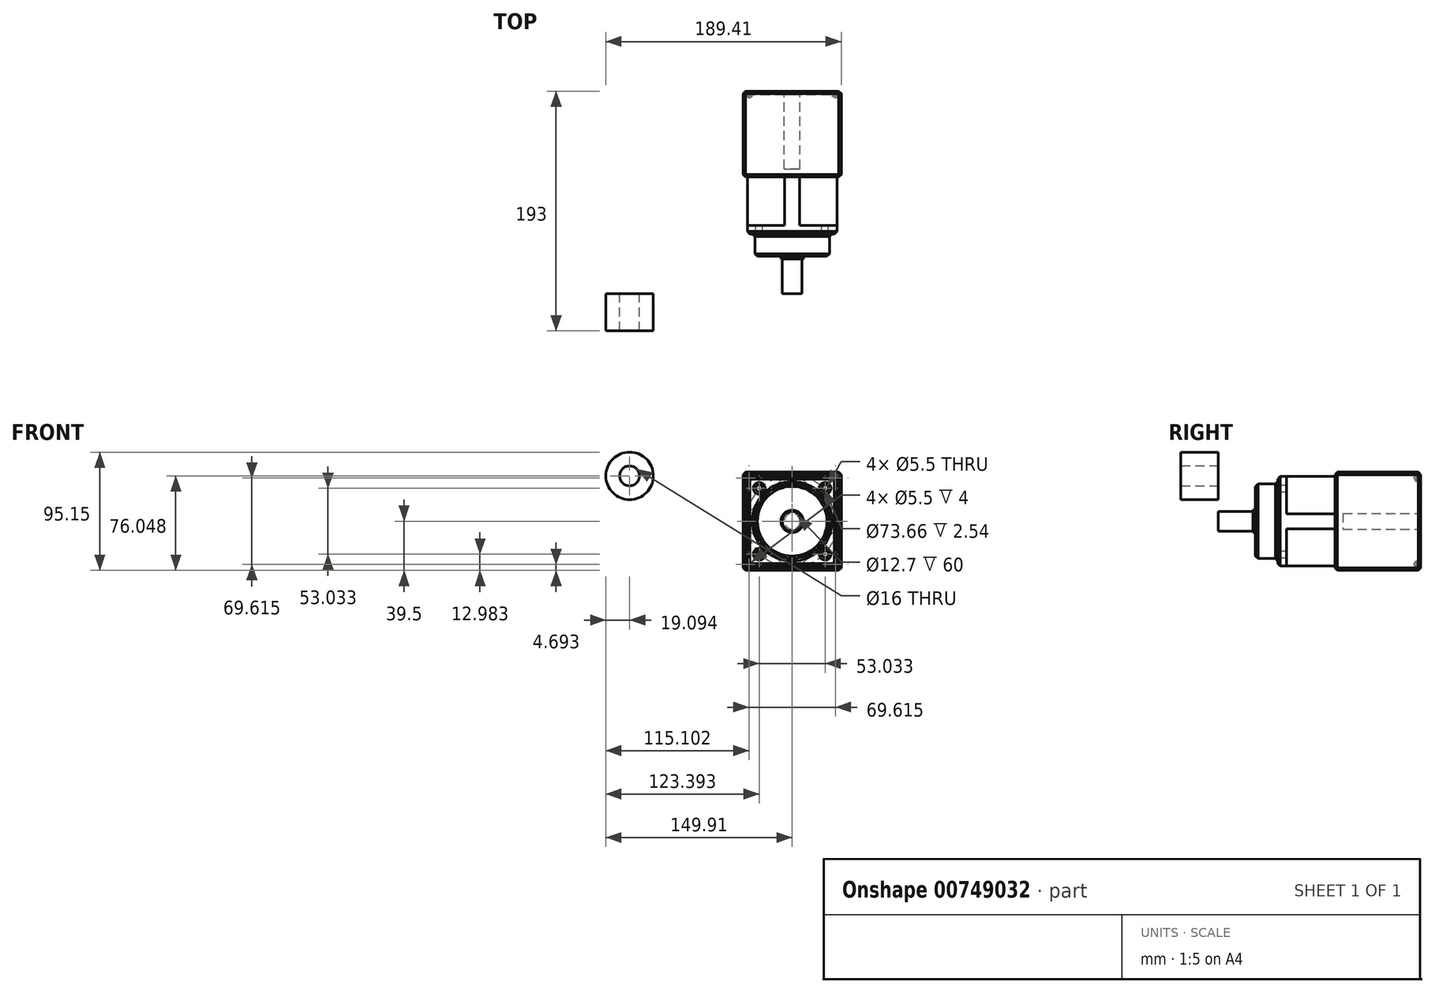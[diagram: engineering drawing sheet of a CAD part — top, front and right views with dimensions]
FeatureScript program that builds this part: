
annotation { "Feature Type Name" : "Feature", "Feature Type Description" : "" }
export const myFeature = defineFeature(function(context is Context, id is Id, definition is map)
    precondition{}
    {
        {
            var Q0;
            Q0=qCreatedBy(makeId("Front.planeOp"),FACE);
            var sketch = newSketch(context, id + "F0", { "sketchPlane" : qUnion([Q0])});
            skCircle(sketch, "E0", {"center": v(0, 0) * mm, "radius": 8 * mm});
            skSolve(sketch);
        }
        {
            var Q0;
            Q0 = qSketchRegion(id + "F0", true);
            extrude(context, id + "F1", {"entities" : qUnion([Q0]), "oppositeDirection" : true, "depth" : 28 * mm, "offsetDistance" : 25 * mm});
        }
        {
            var Q0;
            Q0=makeQuery(id+"F1.opExtrude","CAP_FACE",FACE,{"disambiguationData":[OSD([sQuery(id+"F0.wireOp",EDGE,"E0")])],"isStart":false});
            var sketch = newSketch(context, id + "F2", { "sketchPlane" : qUnion([Q0])});
            skCircle(sketch, "E1", {"center": v(0, 0) * mm, "radius": 9 * mm});
            skSolve(sketch);
        }
        {
            var Q0;
            Q0 = qSketchRegion(id + "F2", true);
            extrude(context, id + "F3", {"entities" : qUnion([Q0]), "operationType" : NewBodyOperationType.ADD, "depth" : 2 * mm, "offsetDistance" : 25 * mm});
        }
        {
            var Q0;
            Q0=makeQuery(id+"F3.opExtrude","CAP_FACE",FACE,{"disambiguationData":[OSD([sQuery(id+"F2.wireOp",EDGE,"E1")])],"isStart":false});
            var sketch = newSketch(context, id + "F4", { "sketchPlane" : qUnion([Q0])});
            skCircle(sketch, "E2", {"center": v(0, 0) * mm, "radius": 30 * mm});
            skSolve(sketch);
        }
        {
            var Q0;
            Q0 = qSketchRegion(id + "F4", true);
            extrude(context, id + "F5", {"entities" : qUnion([Q0]), "operationType" : NewBodyOperationType.ADD, "depth" : 18 * mm, "offsetDistance" : 25 * mm});
        }
        {
            var Q0;
            Q0=makeQuery(id+"F5.opExtrude","CAP_FACE",FACE,{"disambiguationData":[OSD([sQuery(id+"F4.wireOp",EDGE,"E2")])],"isStart":false});
            var sketch = newSketch(context, id + "F6", { "sketchPlane" : qUnion([Q0])});
            skLineSegment(sketch, "E3.bottom", {"start": v(36, -36) * mm, "end": v(-36, -36) * mm});
            skLineSegment(sketch, "E3.top", {"start": v(36, 36) * mm, "end": v(-36, 36) * mm});
            skLineSegment(sketch, "E3.left", {"start": v(36, -36) * mm, "end": v(36, 36) * mm});
            skLineSegment(sketch, "E3.right", {"start": v(-36, -36) * mm, "end": v(-36, 36) * mm});
            skPoint(sketch, "E3.middle", {"position": v(0, 0) * mm});
            skLineSegment(sketch, "E4", {"start": v(0, -36) * mm, "end": v(0, 36) * mm, "construction": true});
            skLineSegment(sketch, "E5", {"start": v(-36, 0) * mm, "end": v(36, 0) * mm, "construction": true});
            skCircle(sketch, "E6", {"center": v(0, 0) * mm, "radius": 37.5 * mm, "construction": true});
            skLineSegment(sketch, "E7", {"start": v(0, 0) * mm, "end": v(-36, 36) * mm, "construction": true});
            skPoint(sketch, "E8", {"position": v(-26.52, 26.52) * mm});
            skPoint(sketch, "E9.MirrorP", {"position": v(26.52, 26.52) * mm});
            skPoint(sketch, "E10.MirrorP", {"position": v(-26.52, -26.52) * mm});
            skPoint(sketch, "E11.MirrorP", {"position": v(26.52, -26.52) * mm});
            skSolve(sketch);
        }
        {
            var Q0;
            Q0 = qSketchRegion(id + "F6", true);
            extrude(context, id + "F7", {"entities" : qUnion([Q0]), "operationType" : NewBodyOperationType.ADD, "depth" : 7 * mm, "offsetDistance" : 25 * mm});
        }
        {
            var Q0;
            Q0=sQuery(id+"F6.wireOp",VERTEX,"E8");
            var Q1;
            Q1=sQuery(id+"F6.wireOp",VERTEX,"E9.MirrorP");
            var Q2;
            Q2=sQuery(id+"F6.wireOp",VERTEX,"E10.MirrorP");
            var Q3;
            Q3=sQuery(id+"F6.wireOp",VERTEX,"E11.MirrorP");
            var Q4;
            Q4=makeQuery(id+"F1.opExtrude","SWEPT_BODY",BODY,{"disambiguationData":[OSD([sQuery(id+"F0.wireOp",EDGE,"E0")])]});
            hole(context, id + "F8", {"style" : HoleStyle.SIMPLE, "endStyle" : HoleEndStyle.THROUGH, "oppositeDirection" : true, "holeDiameter" : 5.5 * mm, "majorDiameter" : 5 * mm, "isTappedThrough" : true, "tappedDepth" : 1.9 * mm, "tapClearance" : 3, "locations" : qUnion([Q0, Q1, Q2, Q3]), "scope" : qUnion([Q4])});
        }
        {
            var Q0;
            Q0=makeQuery(id+"F7.opExtrude","CAP_FACE",FACE,{"disambiguationData":[OSD([sQuery(id+"F6.wireOp",EDGE,"E3.bottom"),sQuery(id+"F6.wireOp",EDGE,"E3.top"),sQuery(id+"F6.wireOp",EDGE,"E3.left"),sQuery(id+"F6.wireOp",EDGE,"E3.right")])],"isStart":false});
            var sketch = newSketch(context, id + "F9", { "sketchPlane" : qUnion([Q0])});
            skLineSegment(sketch, "E12.bottom", {"start": v(-6, -36) * mm, "end": v(6, -36) * mm});
            skLineSegment(sketch, "E12.top", {"start": v(-6, 36) * mm, "end": v(6, 36) * mm});
            skLineSegment(sketch, "E12.left", {"start": v(-36, -6) * mm, "end": v(-36, 6) * mm});
            skLineSegment(sketch, "E12.right", {"start": v(36, -6) * mm, "end": v(36, 6) * mm});
            skPoint(sketch, "E12.middle", {"position": v(0, 0) * mm});
            skLineSegment(sketch, "E13", {"start": v(-36, 6) * mm, "end": v(-6, 36) * mm});
            skPoint(sketch, "E14.orphan", {"position": v(-36, 36) * mm});
            skLineSegment(sketch, "E15.MirrorCS", {"start": v(36, 6) * mm, "end": v(6, 36) * mm});
            skLineSegment(sketch, "E16.MirrorCS", {"start": v(36, -6) * mm, "end": v(6, -36) * mm});
            skLineSegment(sketch, "E17.MirrorCS", {"start": v(-36, -6) * mm, "end": v(-6, -36) * mm});
            skPoint(sketch, "E18.orphan", {"position": v(-36, -36) * mm});
            skPoint(sketch, "E19.orphan", {"position": v(36, -36) * mm});
            skPoint(sketch, "E20.orphan", {"position": v(36, 36) * mm});
            skSolve(sketch);
        }
        {
            var Q0;
            Q0 = qSketchRegion(id + "F9", true);
            extrude(context, id + "F10", {"entities" : qUnion([Q0]), "operationType" : NewBodyOperationType.ADD, "depth" : 39 * mm, "offsetDistance" : 25 * mm});
        }
        {
            var Q0;
            Q0=makeQuery(id+"F10.opExtrude","CAP_FACE",FACE,{"disambiguationData":[OSD([sQuery(id+"F9.wireOp",EDGE,"E12.bottom"),sQuery(id+"F9.wireOp",EDGE,"E12.top"),sQuery(id+"F9.wireOp",EDGE,"E12.left"),sQuery(id+"F9.wireOp",EDGE,"E12.right"),sQuery(id+"F9.wireOp",EDGE,"E13"),sQuery(id+"F9.wireOp",EDGE,"E15.MirrorCS"),sQuery(id+"F9.wireOp",EDGE,"E16.MirrorCS"),sQuery(id+"F9.wireOp",EDGE,"E17.MirrorCS")])],"isStart":false});
            var sketch = newSketch(context, id + "F11", { "sketchPlane" : qUnion([Q0])});
            skLineSegment(sketch, "E21.bottom", {"start": v(39.5, -39.5) * mm, "end": v(-39.5, -39.5) * mm});
            skLineSegment(sketch, "E21.top", {"start": v(39.5, 39.5) * mm, "end": v(-39.5, 39.5) * mm});
            skLineSegment(sketch, "E21.left", {"start": v(39.5, -39.5) * mm, "end": v(39.5, 39.5) * mm});
            skLineSegment(sketch, "E21.right", {"start": v(-39.5, -39.5) * mm, "end": v(-39.5, 39.5) * mm});
            skPoint(sketch, "E21.middle", {"position": v(0, 0) * mm});
            skSolve(sketch);
        }
        {
            var Q0;
            Q0 = qSketchRegion(id + "F11", true);
            extrude(context, id + "F12", {"entities" : qUnion([Q0]), "operationType" : NewBodyOperationType.ADD, "depth" : 69 * mm, "offsetDistance" : 25 * mm});
        }
        {
            var Q0;
            Q0=makeQuery(id+"F12.opExtrude","CAP_FACE",FACE,{"disambiguationData":[OSD([sQuery(id+"F11.wireOp",EDGE,"E21.bottom"),sQuery(id+"F11.wireOp",EDGE,"E21.top"),sQuery(id+"F11.wireOp",EDGE,"E21.left"),sQuery(id+"F11.wireOp",EDGE,"E21.right")])],"isStart":false});
            var sketch = newSketch(context, id + "F13", { "sketchPlane" : qUnion([Q0])});
            skCircle(sketch, "E22", {"center": v(0, 0) * mm, "radius": 49.23 * mm, "construction": true});
            skLineSegment(sketch, "E23", {"start": v(0, 0) * mm, "end": v(-39.5, 39.5) * mm, "construction": true});
            skPoint(sketch, "E24", {"position": v(-34.8, 34.8) * mm});
            skLineSegment(sketch, "E25", {"start": v(-39.5, 0) * mm, "end": v(39.5, 0) * mm, "construction": true});
            skLineSegment(sketch, "E26", {"start": v(0, 39.5) * mm, "end": v(0, -39.5) * mm, "construction": true});
            skPoint(sketch, "E27.MirrorP", {"position": v(34.8, 34.8) * mm});
            skPoint(sketch, "E28.MirrorP", {"position": v(34.8, -34.8) * mm});
            skPoint(sketch, "E29.MirrorP", {"position": v(-34.8, -34.8) * mm});
            skSolve(sketch);
        }
        {
            var Q0;
            Q0=sQuery(id+"F13.wireOp",VERTEX,"E24");
            var Q1;
            Q1=sQuery(id+"F13.wireOp",VERTEX,"E27.MirrorP");
            var Q2;
            Q2=sQuery(id+"F13.wireOp",VERTEX,"E28.MirrorP");
            var Q3;
            Q3=sQuery(id+"F13.wireOp",VERTEX,"E29.MirrorP");
            var Q4;
            Q4=makeQuery(id+"F1.opExtrude","SWEPT_BODY",BODY,{"disambiguationData":[OSD([sQuery(id+"F0.wireOp",EDGE,"E0")])]});
            hole(context, id + "F14", {"style" : HoleStyle.SIMPLE, "endStyle" : HoleEndStyle.BLIND, "holeDiameter" : 5.5 * mm, "majorDiameter" : 5 * mm, "holeDepth" : 4 * mm, "isTappedThrough" : true, "tappedDepth" : 1.9 * mm, "tapClearance" : 3, "locations" : qUnion([Q0, Q1, Q2, Q3]), "scope" : qUnion([Q4])});
        }
        {
            var Q0;
            Q0=makeQuery(id+"F12.opExtrude","SWEPT_FACE",FACE,{"disambiguationData":[OSD([sQuery(id+"F11.wireOp",EDGE,"E21.left")])]});
            var Q1;
            Q1=makeQuery(id+"F12.opExtrude","SWEPT_FACE",FACE,{"disambiguationData":[OSD([sQuery(id+"F11.wireOp",EDGE,"E21.top")])]});
            var Q2;
            Q2=makeQuery(id+"F12.opExtrude","SWEPT_FACE",FACE,{"disambiguationData":[OSD([sQuery(id+"F11.wireOp",EDGE,"E21.right")])]});
            var Q3;
            Q3=makeQuery(id+"F12.opExtrude","SWEPT_FACE",FACE,{"disambiguationData":[OSD([sQuery(id+"F11.wireOp",EDGE,"E21.bottom")])]});
            var Q4;
            Q4=makeQuery(id+"F7.opExtrude","CAP_FACE",FACE,{"disambiguationData":[OSD([sQuery(id+"F6.wireOp",EDGE,"E3.bottom"),sQuery(id+"F6.wireOp",EDGE,"E3.top"),sQuery(id+"F6.wireOp",EDGE,"E3.left"),sQuery(id+"F6.wireOp",EDGE,"E3.right")])],"isStart":true});
            var Q5;
            Q5=makeQuery(id+"F5.opExtrude","CAP_EDGE",EDGE,{"disambiguationData":[OSD([sQuery(id+"F4.wireOp",EDGE,"E2")])],"isStart":true});
            chamfer(context, id + "F15", {"entities" : qUnion([Q0, Q1, Q2, Q3, Q4, Q5]), "width" : 2 * mm, "tangentPropagation" : true});
        }
        {
            var Q0;
            Q0=makeQuery(id+"F12.opExtrude","CAP_FACE",FACE,{"disambiguationData":[OSD([sQuery(id+"F11.wireOp",EDGE,"E21.bottom"),sQuery(id+"F11.wireOp",EDGE,"E21.top"),sQuery(id+"F11.wireOp",EDGE,"E21.left"),sQuery(id+"F11.wireOp",EDGE,"E21.right")])],"isStart":false});
            var sketch = newSketch(context, id + "F16", { "sketchPlane" : qUnion([Q0])});
            skCircle(sketch, "E30", {"center": v(0, 0) * mm, "radius": 36.83 * mm});
            skSolve(sketch);
        }
        {
            var Q0;
            Q0 = qSketchRegion(id + "F16", true);
            extrude(context, id + "F17", {"entities" : qUnion([Q0]), "operationType" : NewBodyOperationType.REMOVE, "oppositeDirection" : true, "depth" : 2.54 * mm, "offsetDistance" : 25 * mm});
        }
        {
            var Q0;
            Q0=makeQuery(id+"F17.boolean.opBoolean","COPY",FACE,{"derivedFrom":makeQuery(id+"F17.opExtrude","CAP_FACE",FACE,{"disambiguationData":[OSD([sQuery(id+"F16.wireOp",EDGE,"E30")])],"isStart":false})});
            var sketch = newSketch(context, id + "F18", { "sketchPlane" : qUnion([Q0])});
            skCircle(sketch, "E31", {"center": v(0, 0) * mm, "radius": 6.35 * mm});
            skSolve(sketch);
        }
        {
            var Q0;
            Q0 = qSketchRegion(id + "F18", true);
            extrude(context, id + "F19", {"entities" : qUnion([Q0]), "operationType" : NewBodyOperationType.REMOVE, "oppositeDirection" : true, "depth" : 60 * mm, "offsetDistance" : 25 * mm});
        }
        {
            var Q0;
            Q0=qCreatedBy(makeId("Front.planeOp"),FACE);
            var sketch = newSketch(context, id + "F20", { "sketchPlane" : qUnion([Q0])});
            skCircle(sketch, "E32", {"center": v(-130.82, 36.55) * mm, "radius": 19.1 * mm});
            skCircle(sketch, "E33", {"center": v(-130.82, 36.55) * mm, "radius": 8 * mm});
            skSolve(sketch);
        }
        {
            var Q0;
            Q0 = qSketchRegion(id + "F20", true);
            extrude(context, id + "F21", {"entities" : qUnion([Q0]), "depth" : 30 * mm, "offsetDistance" : 25 * mm});
        }
    });
